# Revit family: JOIST JAKS_SIDE
name_source: partatom
category: Detail Items
revit_build: Autodesk Revit 2014 (Build: 20130308_1515(x64)
units: mm (PartAtom-declared; Revit-internal decimal feet)

## types (6) — shared parameters
height 1 = 61 mm

## per-type parameters (varying)
| type | Height of base | IN | height |
| DJ65 | 60 mm | 31 mm  [stored 0.101706 ft] | 90 mm |
| DJ45 | 41 mm  [stored 0.134514 ft] | 14 mm  [stored 0.0459318 ft] | 68 mm |
| DJ35 | 31 mm  [stored 0.101706 ft] | 12 mm  [stored 0.0393701 ft] | 51 mm |
| DJ30 | 26 mm | 10 mm  [stored 0.0328084 ft] | 42 mm  [stored 0.137795 ft] |
| DJ25 | 21 mm  [stored 0.0688976 ft] | 10 mm  [stored 0.0328084 ft] | 33 mm |
| DJ20 | 16 mm  [stored 0.0524934 ft] | 8 mm  [stored 0.0262467 ft] | 25 mm  [stored 0.082021 ft] |

note: [stored X ft] marks values corroborated as IEEE doubles in the binary element streams (Revit-internal decimal feet)

## geometry (parser evidence)
native form markers: Sweep x1
no freeform markers — native parametric forms only
